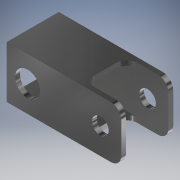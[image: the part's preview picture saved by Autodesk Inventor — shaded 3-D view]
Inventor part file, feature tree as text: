
AUTODESK INVENTOR PART (.ipt)
format: ipt  version: 2018.2 (Build 222227000, 227)  size: 168,960 bytes
history: native  units: mm
features: extrude x5, sketch x5, other x1, fillet x1
ambient origin geometry x8: Origin, YZ Plane, XZ Plane, XY Plane, X Axis, Y Axis, Z Axis, Center Point
bodies: Body1 (feature_tree)
feature tree (12):
  other  "ソリッド1"
  extrude  "押し出し1"  Depth=25.0mm
  extrude  "押し出し2"  Depth=25.0mm
  extrude  "押し出し3"  Depth=55.0mm TaperAngle=0.0deg
  extrude  "押し出し4"  Depth=12.0mm
  extrude  "押し出し5"  Depth=10.0mm
  fillet  "フィレット1"  Radius=12.5mm
  sketch  "スケッチ1"
  sketch  "スケッチ2"
  sketch  "スケッチ3"
  sketch  "スケッチ4"
  sketch  "スケッチ5"
